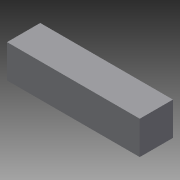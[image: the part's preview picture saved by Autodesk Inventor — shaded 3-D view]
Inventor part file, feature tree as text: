
AUTODESK INVENTOR PART (.ipt)
format: ipt  version: 2015 (Build 190159000, 159)  size: 86,016 bytes
history: native  units: mm
features: extrude x2, sketch x2
ambient origin geometry x8: Origin, YZ Plane, XZ Plane, XY Plane, X Axis, Y Axis, Z Axis, Center Point
bodies: Solid1 (feature_tree)
feature tree (4):
  extrude  "Extrusion1"  Depth=10.0mm
  extrude  "Extrusion2"  Depth=3.0mm
  sketch  "Sketch1"  dims[d0=10.0mm d1=5.2mm]
  sketch  "Sketch2"  dims[d2=5.2mm d3=5.0mm d4=5.0mm d5=40.0mm d6=5.5mm d7=34.5mm d8=7.0mm d9=0.0mm d10=3.0mm d11=0.0mm]
